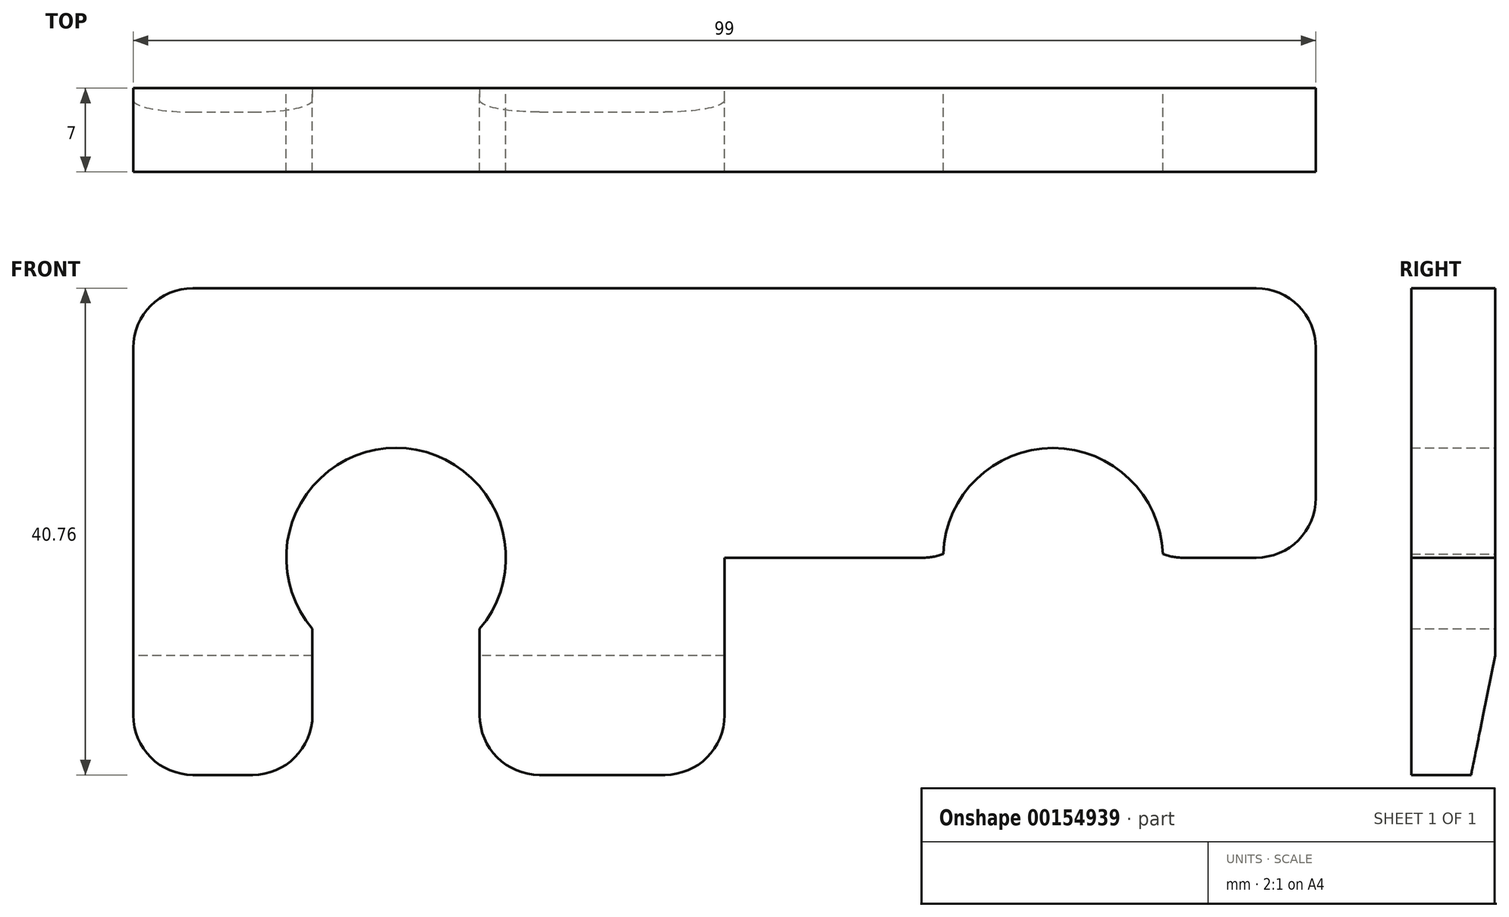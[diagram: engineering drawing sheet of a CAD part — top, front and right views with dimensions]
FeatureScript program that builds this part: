
annotation { "Feature Type Name" : "Feature", "Feature Type Description" : "" }
export const myFeature = defineFeature(function(context is Context, id is Id, definition is map)
    precondition{}
    {
        {
            var Q0;
            Q0=qCreatedBy(makeId("Front.planeOp"),FACE);
            var sketch = newSketch(context, id + "F0", { "sketchPlane" : qUnion([Q0])});
            skLineSegment(sketch, "E0", {"start": v(0, 0) * mm, "end": v(27.5, 0) * mm});
            skArc(sketch, "E1", {"start": v(34.5, 0) * mm, "mid": v(27.5, 7) * mm, "end": v(20.5, 0) * mm});
            skLineSegment(sketch, "E2.bottom", {"start": v(0, 0) * mm, "end": v(49.5, 0) * mm});
            skLineSegment(sketch, "E2.top", {"start": v(0, 22.57) * mm, "end": v(49.5, 22.57) * mm});
            skLineSegment(sketch, "E2.left", {"start": v(0, 0) * mm, "end": v(0, 22.57) * mm});
            skLineSegment(sketch, "E2.right", {"start": v(49.5, 0) * mm, "end": v(49.5, 22.57) * mm});
            skLineSegment(sketch, "E3.bottom", {"start": v(49.5, 0) * mm, "end": v(34.5, 0) * mm});
            skLineSegment(sketch, "E3.top", {"start": v(49.5, -18.19) * mm, "end": v(34.5, -18.19) * mm});
            skLineSegment(sketch, "E3.left", {"start": v(49.5, 0) * mm, "end": v(49.5, -18.19) * mm});
            skLineSegment(sketch, "E3.right", {"start": v(34.5, 0) * mm, "end": v(34.5, -18.19) * mm});
            skLineSegment(sketch, "E4.bottom", {"start": v(0, 0) * mm, "end": v(20.5, 0) * mm});
            skLineSegment(sketch, "E4.top", {"start": v(0, -18.19) * mm, "end": v(20.5, -18.19) * mm});
            skLineSegment(sketch, "E4.left", {"start": v(0, 0) * mm, "end": v(0, -18.19) * mm});
            skLineSegment(sketch, "E4.right", {"start": v(20.5, 0) * mm, "end": v(20.5, -18.19) * mm});
            skLineSegment(sketch, "E5.MirrorCS", {"start": v(0, 0) * mm, "end": v(-27.5, 0) * mm});
            skLineSegment(sketch, "E6.MirrorCS", {"start": v(-49.5, 0) * mm, "end": v(-34.5, 0) * mm});
            skLineSegment(sketch, "E7.MirrorCS", {"start": v(-49.5, 0) * mm, "end": v(-49.5, 22.57) * mm});
            skLineSegment(sketch, "E8.MirrorCS", {"start": v(-49.5, -18.19) * mm, "end": v(-34.5, -18.19) * mm});
            skLineSegment(sketch, "E9.MirrorCS", {"start": v(0, 0) * mm, "end": v(-20.5, 0) * mm});
            skLineSegment(sketch, "E10.MirrorCS", {"start": v(-49.5, 0) * mm, "end": v(-49.5, -18.19) * mm});
            skLineSegment(sketch, "E11.MirrorCS", {"start": v(0, 22.57) * mm, "end": v(-49.5, 22.57) * mm});
            skLineSegment(sketch, "E12.MirrorCS", {"start": v(0, 0) * mm, "end": v(-49.5, 0) * mm});
            skArc(sketch, "E13.MirrorCS", {"start": v(-34.5, 0) * mm, "mid": v(-27.5, 7) * mm, "end": v(-20.5, 0) * mm});
            skLineSegment(sketch, "E14.MirrorCS", {"start": v(-20.5, 0) * mm, "end": v(-20.5, -18.19) * mm});
            skLineSegment(sketch, "E15.MirrorCS", {"start": v(-34.5, 0) * mm, "end": v(-34.5, -18.19) * mm});
            skLineSegment(sketch, "E16.MirrorCS", {"start": v(0, -18.19) * mm, "end": v(-20.5, -18.19) * mm});
            skSolve(sketch);
        }
        {
            var Q0;
            {var subQ2=sQuery(id+"F0.wireOp",EDGE,"E2.left");Q0=makeQuery(id+"F0.imprint","IMPRINT",FACE,{"disambiguationData":[TD([[makeQuery(id+"F0.imprint","IMPRINT",EDGE,{"derivedFrom":subQ2}),1.0]])]});}
            var Q1;
            Q1=makeQuery(id+"F0.imprint","IMPRINT",FACE,{"disambiguationData":[TD([[makeQuery(id+"F0.imprint","IMPRINT",EDGE,{"derivedFrom":sQuery(id+"F0.wireOp",EDGE,"E8.MirrorCS")}),1.0]])]});
            var Q2;
            {var subQ2=sQuery(id+"F0.wireOp",EDGE,"E14.MirrorCS");Q2=makeQuery(id+"F0.imprint","IMPRINT",FACE,{"disambiguationData":[TD([[makeQuery(id+"F0.imprint","IMPRINT",EDGE,{"derivedFrom":subQ2}),1.0]])]});}
            var Q3;
            Q3=makeQuery(id+"F0.imprint","IMPRINT",FACE,{"disambiguationData":[TD([[makeQuery(id+"F0.imprint","IMPRINT",EDGE,{"derivedFrom":sQuery(id+"F0.wireOp",EDGE,"E1")}),-1.0]])]});
            var Q4;
            Q4=makeQuery(id+"F0.imprint","IMPRINT",FACE,{"disambiguationData":[TD([[makeQuery(id+"F0.imprint","IMPRINT",EDGE,{"derivedFrom":sQuery(id+"F0.wireOp",EDGE,"E4.bottom")}),-1.0]])]});
            var Q5;
            Q5=makeQuery(id+"F0.imprint","IMPRINT",FACE,{"disambiguationData":[TD([[makeQuery(id+"F0.imprint","IMPRINT",EDGE,{"derivedFrom":sQuery(id+"F0.wireOp",EDGE,"E3.bottom")}),1.0]])]});
            extrude(context, id + "F1", {"entities" : qUnion([Q0, Q1, Q2, Q3, Q4, Q5]), "depth" : 7 * mm});
        }
        {
            var Q0;
            Q0=qCreatedBy(makeId("Right.planeOp"),FACE);
            var sketch = newSketch(context, id + "F2", { "sketchPlane" : qUnion([Q0])});
            skPoint(sketch, "E17.0", {"position": v(0, 22.57) * mm});
            skLineSegment(sketch, "E18.0", {"start": v(0, 0) * mm, "end": v(0, 7) * mm});
            skPoint(sketch, "E19.0", {"position": v(-7, 22.57) * mm});
            skFitSpline(sketch, "E20", {"points": [v(-7, 22.57) * mm, v(-1.22, 28.8) * mm, v(8.78, 30.68) * mm, v(10.24, 26.72) * mm, v(6.38, 28.46) * mm, v(0.68, 26.2) * mm, v(0, 22.57) * mm], "startDerivative": vector(1.67, 33.67) * mm, "endDerivative": vector(-3.85, -28.78) * mm});
            skLineSegment(sketch, "E21", {"start": v(0, 22.57) * mm, "end": v(-7, 22.57) * mm});
            skSolve(sketch);
        }
        {
            var Q0;
            Q0=makeQuery(id+"F1.opExtrude","CAP_EDGE",EDGE,{"disambiguationData":[OSD([sQuery(id+"F0.wireOp",EDGE,"E4.top"),sQuery(id+"F0.wireOp",EDGE,"E16.MirrorCS")])],"isStart":true});
            var Q1;
            Q1=makeQuery(id+"F1.opExtrude","CAP_EDGE",EDGE,{"disambiguationData":[OSD([sQuery(id+"F0.wireOp",EDGE,"E3.top")])],"isStart":true});
            var Q2;
            Q2=makeQuery(id+"F1.opExtrude","CAP_EDGE",EDGE,{"disambiguationData":[OSD([sQuery(id+"F0.wireOp",EDGE,"E8.MirrorCS")])],"isStart":true});
            chamfer(context, id + "F3", {"entities" : qUnion([Q0, Q1, Q2]), "chamferType" : ChamferType.TWO_OFFSETS, "width1" : 10 * mm, "oppositeDirection" : false, "width2" : 2 * mm, "tangentPropagation" : true});
        }
        {
            var Q0;
            Q0=makeQuery(id+"F1.opExtrude","SWEPT_EDGE",EDGE,{"disambiguationData":[OSD([sQuery(id+"F0.wireOp",EDGE,"E14.MirrorCS"),sQuery(id+"F0.wireOp",EDGE,"E16.MirrorCS")])]});
            var Q1;
            Q1=makeQuery(id+"F1.opExtrude","SWEPT_EDGE",EDGE,{"disambiguationData":[OSD([sQuery(id+"F0.wireOp",EDGE,"E8.MirrorCS"),sQuery(id+"F0.wireOp",EDGE,"E15.MirrorCS")])]});
            var Q2;
            Q2=makeQuery(id+"F1.opExtrude","SWEPT_EDGE",EDGE,{"disambiguationData":[OSD([sQuery(id+"F0.wireOp",EDGE,"E4.top"),sQuery(id+"F0.wireOp",EDGE,"E4.right")])]});
            var Q3;
            Q3=makeQuery(id+"F1.opExtrude","SWEPT_EDGE",EDGE,{"disambiguationData":[OSD([sQuery(id+"F0.wireOp",EDGE,"E3.top"),sQuery(id+"F0.wireOp",EDGE,"E3.right")])]});
            var Q4;
            Q4=makeQuery(id+"F1.opExtrude","SWEPT_EDGE",EDGE,{"disambiguationData":[OSD([sQuery(id+"F0.wireOp",EDGE,"E3.top"),sQuery(id+"F0.wireOp",EDGE,"E3.left")])]});
            var Q5;
            Q5=makeQuery(id+"F1.opExtrude","SWEPT_EDGE",EDGE,{"disambiguationData":[OSD([sQuery(id+"F0.wireOp",EDGE,"E8.MirrorCS"),sQuery(id+"F0.wireOp",EDGE,"E10.MirrorCS")])]});
            fillet(context, id + "F4", {"entities" : qUnion([Q0, Q1, Q2, Q3, Q4, Q5]), "radius" : 5 * mm, "tangentPropagation" : true, "allowEdgeOverflow" : false});
        }
        {
            var Q0;
            Q0=qCreatedBy(makeId("Front.planeOp"),FACE);
            var sketch = newSketch(context, id + "F5", { "sketchPlane" : qUnion([Q0])});
            skPoint(sketch, "E22.0", {"position": v(27.5, 0) * mm});
            skPoint(sketch, "E23.0", {"position": v(-27.5, 0) * mm});
            skCircle(sketch, "E24", {"center": v(27.5, 0) * mm, "radius": 9.2 * mm});
            skCircle(sketch, "E25", {"center": v(-27.5, 0) * mm, "radius": 9.2 * mm});
            skSolve(sketch);
        }
        {
            var Q0;
            Q0=makeQuery(id+"F5.imprint","IMPRINT",FACE,{"disambiguationData":[TD([[makeQuery(id+"F5.imprint","IMPRINT",EDGE,{"derivedFrom":sQuery(id+"F5.wireOp",EDGE,"E25")}),1.0]])]});
            var Q1;
            Q1=makeQuery(id+"F5.imprint","IMPRINT",FACE,{"disambiguationData":[TD([[makeQuery(id+"F5.imprint","IMPRINT",EDGE,{"derivedFrom":sQuery(id+"F5.wireOp",EDGE,"E24")}),1.0]])]});
            var Q2;
            Q2=makeQuery(id+"F1.opExtrude","CAP_FACE",FACE,{"disambiguationData":[OSD([sQuery(id+"F0.wireOp",EDGE,"E1"),sQuery(id+"F0.wireOp",EDGE,"E2.top"),sQuery(id+"F0.wireOp",EDGE,"E2.right"),sQuery(id+"F0.wireOp",EDGE,"E3.top"),sQuery(id+"F0.wireOp",EDGE,"E3.left"),sQuery(id+"F0.wireOp",EDGE,"E3.right"),sQuery(id+"F0.wireOp",EDGE,"E4.top"),sQuery(id+"F0.wireOp",EDGE,"E4.right"),sQuery(id+"F0.wireOp",EDGE,"E7.MirrorCS"),sQuery(id+"F0.wireOp",EDGE,"E8.MirrorCS"),sQuery(id+"F0.wireOp",EDGE,"E10.MirrorCS"),sQuery(id+"F0.wireOp",EDGE,"E11.MirrorCS"),sQuery(id+"F0.wireOp",EDGE,"E13.MirrorCS"),sQuery(id+"F0.wireOp",EDGE,"E14.MirrorCS"),sQuery(id+"F0.wireOp",EDGE,"E15.MirrorCS"),sQuery(id+"F0.wireOp",EDGE,"E16.MirrorCS")])],"isStart":false});
            extrude(context, id + "F6", {"entities" : qUnion([Q0, Q1]), "operationType" : NewBodyOperationType.REMOVE, "endBound" : BoundingType.UP_TO_SURFACE, "endBoundEntityFace" : qUnion([Q2]), "depth" : 25 * mm});
        }
        {
            var Q0;
            Q0=makeQuery(id+"F1.opExtrude","SWEPT_EDGE",EDGE,{"disambiguationData":[OSD([sQuery(id+"F0.wireOp",EDGE,"E7.MirrorCS"),sQuery(id+"F0.wireOp",EDGE,"E11.MirrorCS")])]});
            var Q1;
            Q1=makeQuery(id+"F1.opExtrude","SWEPT_EDGE",EDGE,{"disambiguationData":[OSD([sQuery(id+"F0.wireOp",EDGE,"E2.top"),sQuery(id+"F0.wireOp",EDGE,"E2.right")])]});
            fillet(context, id + "F7", {"entities" : qUnion([Q0, Q1]), "radius" : 5 * mm, "tangentPropagation" : true, "allowEdgeOverflow" : false});
        }
    });
